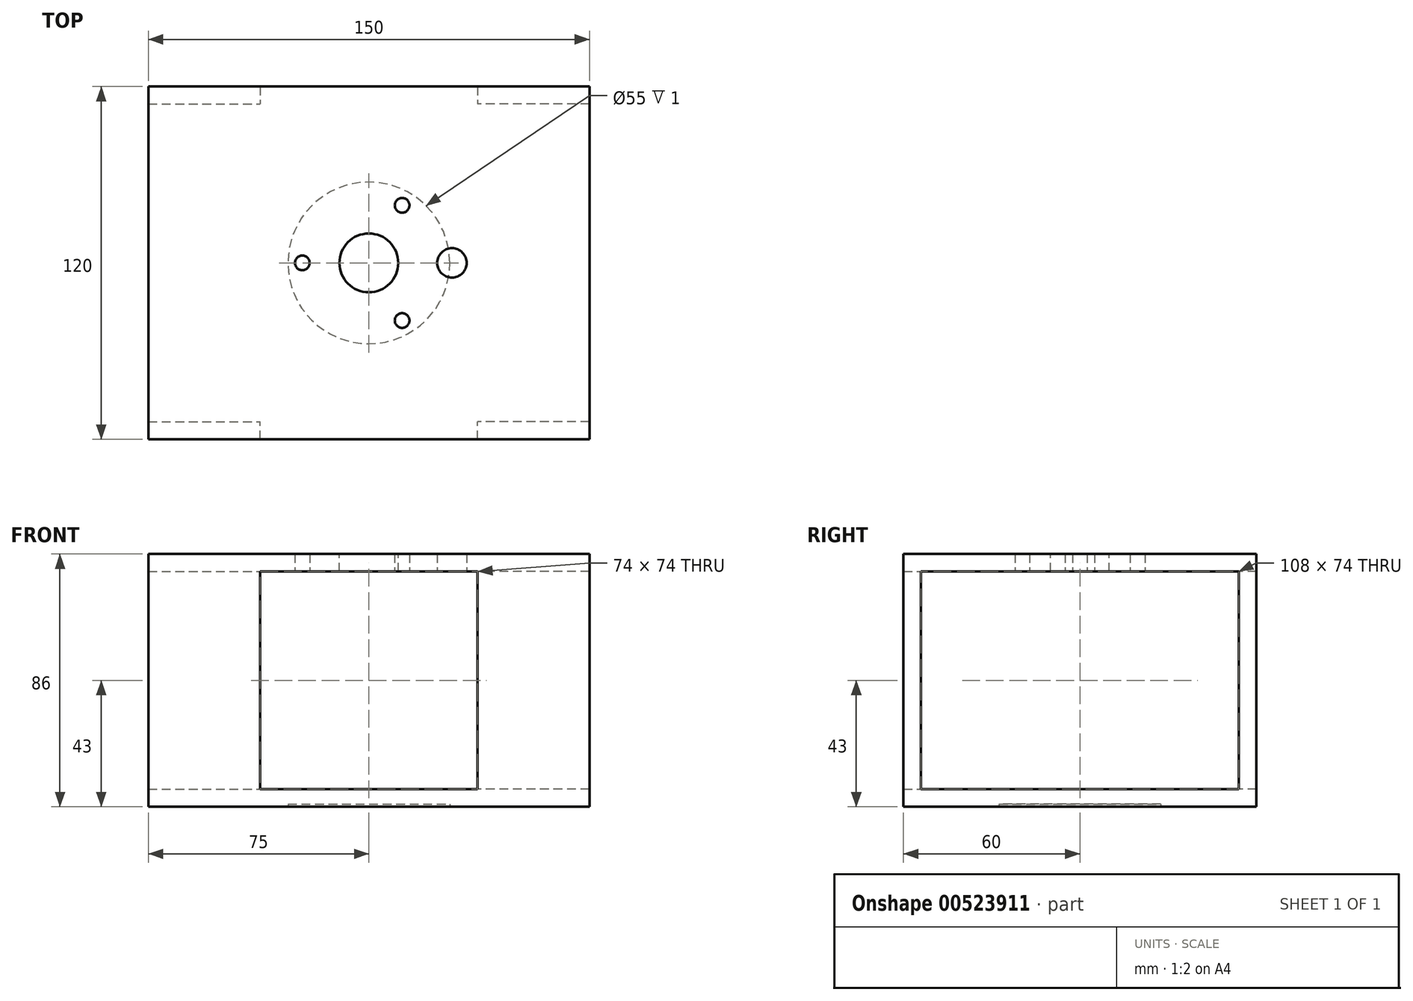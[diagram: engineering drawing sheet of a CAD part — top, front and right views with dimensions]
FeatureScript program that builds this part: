
annotation { "Feature Type Name" : "Feature", "Feature Type Description" : "" }
export const myFeature = defineFeature(function(context is Context, id is Id, definition is map)
    precondition{}
    {
        {
            var Q0;
            Q0=qCreatedBy(makeId("Top.planeOp"),FACE);
            var sketch = newSketch(context, id + "F0", { "sketchPlane" : qUnion([Q0])});
            skCircle(sketch, "E0", {"center": v(0, 0) * mm, "radius": 22.63 * mm});
            skCircle(sketch, "E1", {"center": v(-22.63, 0) * mm, "radius": 2.5 * mm});
            skCircle(sketch, "E2", {"center": v(0, 0) * mm, "radius": 50 * mm});
            skLineSegment(sketch, "E3.bottom", {"start": v(-75, 60) * mm, "end": v(75, 60) * mm});
            skLineSegment(sketch, "E3.top", {"start": v(-75, -60) * mm, "end": v(75, -60) * mm});
            skLineSegment(sketch, "E3.left", {"start": v(-75, 60) * mm, "end": v(-75, -60) * mm});
            skLineSegment(sketch, "E3.right", {"start": v(75, 60) * mm, "end": v(75, -60) * mm});
            skCircle(sketch, "E4", {"center": v(28.27, 0) * mm, "radius": 5 * mm});
            skSolve(sketch);
        }
        {
            var Q0;
            Q0=makeQuery(id+"F0.imprint","IMPRINT",FACE,{"disambiguationData":[TD([[makeQuery(id+"F0.imprint","IMPRINT",EDGE,{"derivedFrom":sQuery(id+"F0.wireOp",EDGE,"E1")}),1.0]])]});
            extrude(context, id + "F1", {"entities" : qUnion([Q0]), "oppositeDirection" : true, "depth" : 25 * mm, "offsetDistance" : 25 * mm});
        }
        {
            var Q0;
            Q0=qCreatedBy(makeId("Front.planeOp"),FACE);
            var sketch = newSketch(context, id + "F2", { "sketchPlane" : qUnion([Q0])});
            skLineSegment(sketch, "E5", {"start": v(0, 0) * mm, "end": v(0, 62.76) * mm});
            skSolve(sketch);
        }
        {
            var Q0;
            Q0 = qSketchRegion(id + "F0", true);
            var Q1;
            {var subQ0=sQuery(id+"F0.wireOp",EDGE,"E1");var subQ1=sQuery(id+"F0.wireOp",EDGE,"E0");var subQ2=makeQuery(id+"F0.imprint","INTERSECT",VERTEX,{"disambiguationData":[OD(0.0)],"derivedFrom":[subQ1,subQ0]});Q1=makeQuery(id+"F0.imprint","IMPRINT",FACE,{"disambiguationData":[TD([[makeQuery(id+"F0.imprint","IMPRINT",EDGE,{"disambiguationData":[TD([[subQ2,1.0]])],"derivedFrom":subQ1}),-1.0]])]});}
            var Q2;
            {var subQ0=sQuery(id+"F0.wireOp",EDGE,"E1");var subQ1=sQuery(id+"F0.wireOp",EDGE,"E0");var subQ2=makeQuery(id+"F0.imprint","INTERSECT",VERTEX,{"disambiguationData":[OD(0.0)],"derivedFrom":[subQ1,subQ0]});Q2=makeQuery(id+"F0.imprint","IMPRINT",FACE,{"disambiguationData":[TD([[makeQuery(id+"F0.imprint","IMPRINT",EDGE,{"disambiguationData":[TD([[subQ2,-1.0]])],"derivedFrom":subQ1}),1.0]])]});}
            var Q3;
            {var subQ0=sQuery(id+"F0.wireOp",EDGE,"E1");var subQ1=sQuery(id+"F0.wireOp",EDGE,"E0");var subQ2=makeQuery(id+"F0.imprint","INTERSECT",VERTEX,{"disambiguationData":[OD(0.0)],"derivedFrom":[subQ1,subQ0]});Q3=makeQuery(id+"F0.imprint","IMPRINT",FACE,{"disambiguationData":[TD([[makeQuery(id+"F0.imprint","IMPRINT",EDGE,{"disambiguationData":[TD([[subQ2,1.0]])],"derivedFrom":subQ1}),1.0]])]});}
            var Q4;
            Q4=makeQuery(id+"F0.imprint","IMPRINT",FACE,{"disambiguationData":[TD([[makeQuery(id+"F0.imprint","IMPRINT",EDGE,{"derivedFrom":sQuery(id+"F0.wireOp",EDGE,"E2")}),1.0]])]});
            extrude(context, id + "F3", {"entities" : qUnion([Q0, Q1, Q2, Q3, Q4]), "depth" : 6 * mm, "offsetDistance" : 25 * mm});
        }
        {
            var Q0;
            Q0=makeQuery(id+"F1.opExtrude","SWEPT_BODY",BODY,{"disambiguationData":[OSD([sQuery(id+"F0.wireOp",EDGE,"E1")])]});
            var Q1;
            Q1=sQuery(id+"F2.wireOp",EDGE,"E5");
            circularPattern(context, id + "F4", {"entities" : qUnion([Q0]), "axis" : qUnion([Q1]), "angle" : 360 * degree, "instanceCount" : 3, "equalSpace" : true, "isCentered" : true});
        }
        {
            var Q0;
            Q0=makeQuery(id+"F4.opPattern","COPY",FACE,{"derivedFrom":makeQuery(id+"F1.opExtrude","CAP_FACE",FACE,{"disambiguationData":[OSD([sQuery(id+"F0.wireOp",EDGE,"E1")])],"isStart":false}),"instanceName":"1"});
            var Q1;
            Q1=makeQuery(id+"F1.opExtrude","CAP_FACE",FACE,{"disambiguationData":[OSD([sQuery(id+"F0.wireOp",EDGE,"E1")])],"isStart":false});
            var Q2;
            Q2=makeQuery(id+"F4.opPattern","COPY",FACE,{"derivedFrom":makeQuery(id+"F1.opExtrude","CAP_FACE",FACE,{"disambiguationData":[OSD([sQuery(id+"F0.wireOp",EDGE,"E1")])],"isStart":false}),"instanceName":"-1"});
            extrude(context, id + "F5", {"entities" : qUnion([Q0, Q1, Q2]), "operationType" : NewBodyOperationType.REMOVE, "oppositeDirection" : true, "depth" : 100 * mm, "offsetDistance" : 25 * mm, "hasSecondDirection" : true, "secondDirectionOppositeDirection" : false, "secondDirectionDepth" : 25 * mm});
        }
        {
            var Q0;
            Q0=makeQuery(id+"F3.opExtrude","CAP_FACE",FACE,{"disambiguationData":[OSD([sQuery(id+"F0.wireOp",EDGE,"E3.bottom"),sQuery(id+"F0.wireOp",EDGE,"E3.top"),sQuery(id+"F0.wireOp",EDGE,"E3.left"),sQuery(id+"F0.wireOp",EDGE,"E3.right")])],"isStart":false});
            var sketch = newSketch(context, id + "F6", { "sketchPlane" : qUnion([Q0])});
            skCircle(sketch, "E6", {"center": v(0, 0) * mm, "radius": 10 * mm});
            skSolve(sketch);
        }
        {
            var Q0;
            Q0 = qSketchRegion(id + "F6", true);
            extrude(context, id + "F7", {"entities" : qUnion([Q0]), "operationType" : NewBodyOperationType.REMOVE, "oppositeDirection" : true, "depth" : 25 * mm, "offsetDistance" : 25 * mm});
        }
        {
            var Q0;
            Q0=makeQuery(id+"F3.opExtrude","CAP_FACE",FACE,{"disambiguationData":[OSD([sQuery(id+"F0.wireOp",EDGE,"E3.bottom"),sQuery(id+"F0.wireOp",EDGE,"E3.top"),sQuery(id+"F0.wireOp",EDGE,"E3.left"),sQuery(id+"F0.wireOp",EDGE,"E3.right")])],"isStart":false});
            var sketch = newSketch(context, id + "F8", { "sketchPlane" : qUnion([Q0])});
            skLineSegment(sketch, "E7.bottom", {"start": v(-75, 60) * mm, "end": v(-37, 60) * mm});
            skLineSegment(sketch, "E7.top", {"start": v(-75, 54) * mm, "end": v(-37, 54) * mm});
            skLineSegment(sketch, "E7.left", {"start": v(-75, 60) * mm, "end": v(-75, 54) * mm});
            skLineSegment(sketch, "E7.right", {"start": v(-37, 60) * mm, "end": v(-37, 54) * mm});
            skLineSegment(sketch, "E8.bottom", {"start": v(-75, -60) * mm, "end": v(-37, -60) * mm});
            skLineSegment(sketch, "E8.top", {"start": v(-75, -54) * mm, "end": v(-37, -54) * mm});
            skLineSegment(sketch, "E8.left", {"start": v(-75, -60) * mm, "end": v(-75, -54) * mm});
            skLineSegment(sketch, "E8.right", {"start": v(-37, -60) * mm, "end": v(-37, -54) * mm});
            skPoint(sketch, "E9.oppositeSnap0", {"position": v(-56, -54) * mm});
            skLineSegment(sketch, "E9.bottom", {"start": v(75, -60) * mm, "end": v(37, -60) * mm});
            skLineSegment(sketch, "E9.top", {"start": v(75, -54) * mm, "end": v(37, -54) * mm});
            skLineSegment(sketch, "E9.left", {"start": v(75, -60) * mm, "end": v(75, -54) * mm});
            skLineSegment(sketch, "E9.right", {"start": v(37, -60) * mm, "end": v(37, -54) * mm});
            skLineSegment(sketch, "E10.bottom", {"start": v(75, 60) * mm, "end": v(37, 60) * mm});
            skLineSegment(sketch, "E10.top", {"start": v(75, 54) * mm, "end": v(37, 54) * mm});
            skLineSegment(sketch, "E10.left", {"start": v(75, 60) * mm, "end": v(75, 54) * mm});
            skLineSegment(sketch, "E10.right", {"start": v(37, 60) * mm, "end": v(37, 54) * mm});
            skSolve(sketch);
        }
        {
            var Q0;
            Q0=makeQuery(id+"F8.imprint","IMPRINT",FACE,{"disambiguationData":[TD([[makeQuery(id+"F8.imprint","IMPRINT",EDGE,{"derivedFrom":sQuery(id+"F8.wireOp",EDGE,"E7.bottom")}),-1.0]])]});
            var Q1;
            Q1=makeQuery(id+"F8.imprint","IMPRINT",FACE,{"disambiguationData":[TD([[makeQuery(id+"F8.imprint","IMPRINT",EDGE,{"derivedFrom":sQuery(id+"F8.wireOp",EDGE,"E10.bottom")}),-1.0]])]});
            var Q2;
            Q2=makeQuery(id+"F8.imprint","IMPRINT",FACE,{"disambiguationData":[TD([[makeQuery(id+"F8.imprint","IMPRINT",EDGE,{"derivedFrom":sQuery(id+"F8.wireOp",EDGE,"E9.bottom")}),1.0]])]});
            var Q3;
            Q3=makeQuery(id+"F8.imprint","IMPRINT",FACE,{"disambiguationData":[TD([[makeQuery(id+"F8.imprint","IMPRINT",EDGE,{"derivedFrom":sQuery(id+"F8.wireOp",EDGE,"E8.bottom")}),1.0]])]});
            var Q4;
            Q4=makeQuery(id+"F8.imprint","IMPRINT",FACE,{"disambiguationData":[TD([[makeQuery(id+"F8.imprint","IMPRINT",EDGE,{"derivedFrom":sQuery(id+"F8.wireOp",EDGE,"IISYLC2l-fWnh-Ak6s-lzwn-dIzXM5EjJxJh.bottom")}),1.0]])]});
            var Q5;
            Q5=makeQuery(id+"F8.imprint","IMPRINT",FACE,{"disambiguationData":[TD([[makeQuery(id+"F8.imprint","IMPRINT",EDGE,{"derivedFrom":sQuery(id+"F8.wireOp",EDGE,"MjN5Hxp7-mmXw-y8nL-TM7P-fzvtC5XdUNCU.bottom")}),-1.0]])]});
            extrude(context, id + "F9", {"entities" : qUnion([Q0, Q1, Q2, Q3, Q4, Q5]), "operationType" : NewBodyOperationType.ADD, "oppositeDirection" : true, "depth" : 80 * mm, "offsetDistance" : 25 * mm});
        }
        {
            var Q0;
            Q0=makeQuery(id+"F9.opExtrude","CAP_FACE",FACE,{"disambiguationData":[OSD([sQuery(id+"F8.wireOp",EDGE,"E8.bottom"),sQuery(id+"F8.wireOp",EDGE,"E8.top"),sQuery(id+"F8.wireOp",EDGE,"E8.left"),sQuery(id+"F8.wireOp",EDGE,"E8.right")])],"isStart":false});
            var sketch = newSketch(context, id + "F10", { "sketchPlane" : qUnion([Q0])});
            skLineSegment(sketch, "E11.bottom", {"start": v(-75, 60) * mm, "end": v(75, 60) * mm});
            skLineSegment(sketch, "E11.top", {"start": v(-75, -60) * mm, "end": v(75, -60) * mm});
            skLineSegment(sketch, "E11.left", {"start": v(-75, 60) * mm, "end": v(-75, -60) * mm});
            skLineSegment(sketch, "E11.right", {"start": v(75, 60) * mm, "end": v(75, -60) * mm});
            skSolve(sketch);
        }
        {
            var Q0;
            Q0 = qSketchRegion(id + "F10", true);
            extrude(context, id + "F11", {"entities" : qUnion([Q0]), "operationType" : NewBodyOperationType.ADD, "depth" : 6 * mm, "offsetDistance" : 25 * mm});
        }
        {
            var Q0;
            Q0=makeQuery(id+"F11.opExtrude","CAP_FACE",FACE,{"disambiguationData":[OSD([sQuery(id+"F10.wireOp",EDGE,"E11.bottom"),sQuery(id+"F10.wireOp",EDGE,"E11.top"),sQuery(id+"F10.wireOp",EDGE,"E11.left"),sQuery(id+"F10.wireOp",EDGE,"E11.right")])],"isStart":false});
            var sketch = newSketch(context, id + "F12", { "sketchPlane" : qUnion([Q0])});
            skCircle(sketch, "E12", {"center": v(0, 0) * mm, "radius": 27.5 * mm});
            skSolve(sketch);
        }
        {
            var Q0;
            Q0=makeQuery(id+"F12.imprint","IMPRINT",FACE,{"disambiguationData":[TD([[makeQuery(id+"F12.imprint","IMPRINT",EDGE,{"derivedFrom":sQuery(id+"F12.wireOp",EDGE,"E12")}),1.0]])]});
            extrude(context, id + "F13", {"entities" : qUnion([Q0]), "operationType" : NewBodyOperationType.REMOVE, "oppositeDirection" : true, "depth" : 1 * mm, "offsetDistance" : 25 * mm});
        }
    });
